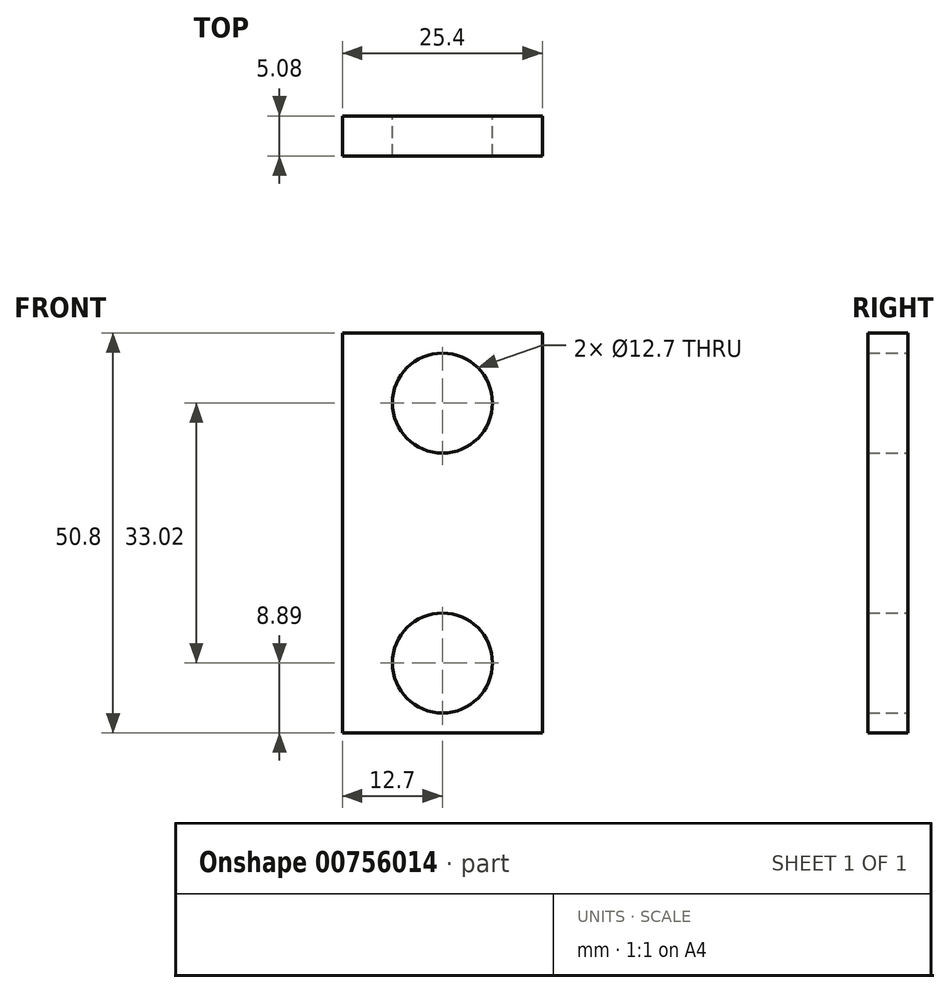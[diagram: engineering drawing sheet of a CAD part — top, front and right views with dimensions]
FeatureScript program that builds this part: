
annotation { "Feature Type Name" : "Feature", "Feature Type Description" : "" }
export const myFeature = defineFeature(function(context is Context, id is Id, definition is map)
    precondition{}
    {
        {
            var Q0;
            Q0=qCreatedBy(makeId("Front.planeOp"),FACE);
            var sketch = newSketch(context, id + "F0", { "sketchPlane" : qUnion([Q0])});
            skLineSegment(sketch, "E0.bottom", {"start": v(-12.7, 25.4) * mm, "end": v(12.7, 25.4) * mm});
            skLineSegment(sketch, "E0.top", {"start": v(-12.7, -25.4) * mm, "end": v(12.7, -25.4) * mm});
            skLineSegment(sketch, "E0.left", {"start": v(-12.7, 25.4) * mm, "end": v(-12.7, -25.4) * mm});
            skLineSegment(sketch, "E0.right", {"start": v(12.7, 25.4) * mm, "end": v(12.7, -25.4) * mm});
            skPoint(sketch, "E0.middle", {"position": v(0, 0) * mm});
            skCircle(sketch, "E1", {"center": v(0, 16.51) * mm, "radius": 6.35 * mm});
            skCircle(sketch, "E2", {"center": v(0, -16.5) * mm, "radius": 6.35 * mm});
            skSolve(sketch);
        }
        {
            var Q0;
            Q0=makeQuery(id+"F0.imprint","IMPRINT",FACE,{"disambiguationData":[TD([[makeQuery(id+"F0.imprint","IMPRINT",EDGE,{"derivedFrom":sQuery(id+"F0.wireOp",EDGE,"E0.bottom")}),-1.0]])]});
            extrude(context, id + "F1", {"entities" : qUnion([Q0]), "depth" : 5.08 * mm, "offsetDistance" : 25.4 * mm});
        }
    });
